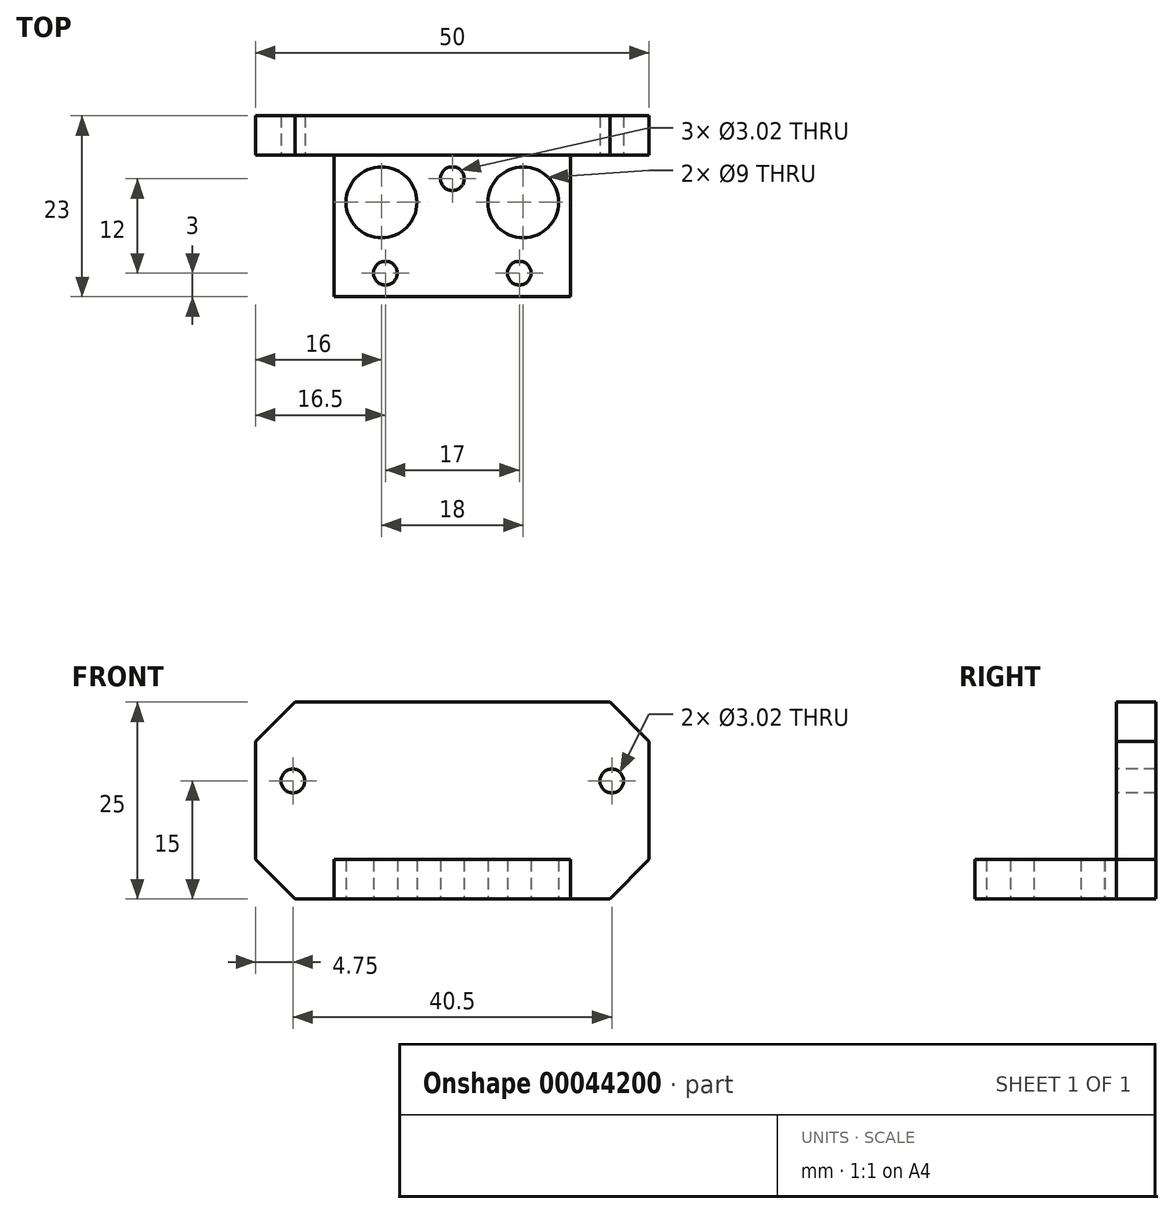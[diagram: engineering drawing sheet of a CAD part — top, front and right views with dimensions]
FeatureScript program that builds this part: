
annotation { "Feature Type Name" : "Feature", "Feature Type Description" : "" }
export const myFeature = defineFeature(function(context is Context, id is Id, definition is map)
    precondition{}
    {
        {
            var Q0;
            Q0=qCreatedBy(makeId("Top.planeOp"),FACE);
            var sketch = newSketch(context, id + "F0", { "sketchPlane" : qUnion([Q0])});
            skLineSegment(sketch, "E0.bottom", {"start": v(0, 0) * mm, "end": v(30, 0) * mm});
            skLineSegment(sketch, "E0.top", {"start": v(0, 18) * mm, "end": v(30, 18) * mm, "construction": true});
            skLineSegment(sketch, "E0.left", {"start": v(0, 0) * mm, "end": v(0, 18) * mm});
            skLineSegment(sketch, "E0.right", {"start": v(30, 0) * mm, "end": v(30, 18) * mm});
            skLineSegment(sketch, "E1", {"start": v(15, 18) * mm, "end": v(15, 15) * mm, "construction": true});
            skCircle(sketch, "E2", {"center": v(15, 15) * mm, "radius": 1.51 * mm});
            skLineSegment(sketch, "E3", {"start": v(15, 15) * mm, "end": v(15, 3) * mm, "construction": true});
            skLineSegment(sketch, "E4", {"start": v(15, 3) * mm, "end": v(23.5, 3) * mm, "construction": true});
            skLineSegment(sketch, "E5", {"start": v(15, 3) * mm, "end": v(6.5, 3) * mm, "construction": true});
            skLineSegment(sketch, "E6", {"start": v(15, 12) * mm, "end": v(24, 12) * mm, "construction": true});
            skLineSegment(sketch, "E7", {"start": v(15, 12) * mm, "end": v(6, 12) * mm, "construction": true});
            skLineSegment(sketch, "E8", {"start": v(24, 12) * mm, "end": v(24, 18) * mm, "construction": true});
            skCircle(sketch, "E9", {"center": v(6, 12) * mm, "radius": 4.5 * mm});
            skCircle(sketch, "E10", {"center": v(24, 12) * mm, "radius": 4.5 * mm});
            skCircle(sketch, "E11", {"center": v(23.5, 3) * mm, "radius": 1.51 * mm});
            skCircle(sketch, "E12", {"center": v(6.5, 3) * mm, "radius": 1.51 * mm});
            skLineSegment(sketch, "E13", {"start": v(0, 18) * mm, "end": v(0, 23) * mm});
            skLineSegment(sketch, "E14", {"start": v(0, 23) * mm, "end": v(29.76, 23) * mm});
            skLineSegment(sketch, "E15", {"start": v(29.76, 23) * mm, "end": v(30, 23) * mm});
            skLineSegment(sketch, "E16", {"start": v(30, 23) * mm, "end": v(30, 18) * mm});
            skSolve(sketch);
        }
        {
            var Q0;
            Q0 = qSketchRegion(id + "F0", true);
            var Q1;
            Q1=makeQuery(id+"F0.imprint","IMPRINT",FACE,{"disambiguationData":[TD([[makeQuery(id+"F0.imprint","IMPRINT",EDGE,{"derivedFrom":sQuery(id+"F0.wireOp",EDGE,"E0.bottom")}),1.0]])]});
            extrude(context, id + "F1", {"entities" : qUnion([Q0, Q1]), "depth" : 5 * mm});
        }
        {
            var Q0;
            Q0=makeQuery(id+"F1.opExtrude","CAP_FACE",FACE,{"disambiguationData":[OSD([sQuery(id+"F0.wireOp",EDGE,"E0.bottom"),sQuery(id+"F0.wireOp",EDGE,"E0.left"),sQuery(id+"F0.wireOp",EDGE,"E0.right"),sQuery(id+"F0.wireOp",EDGE,"E2"),sQuery(id+"F0.wireOp",EDGE,"E9"),sQuery(id+"F0.wireOp",EDGE,"E10"),sQuery(id+"F0.wireOp",EDGE,"E11"),sQuery(id+"F0.wireOp",EDGE,"E12"),sQuery(id+"F0.wireOp",EDGE,"E13"),sQuery(id+"F0.wireOp",EDGE,"E14"),sQuery(id+"F0.wireOp",EDGE,"E15"),sQuery(id+"F0.wireOp",EDGE,"E16")])],"isStart":false});
            var sketch = newSketch(context, id + "F2", { "sketchPlane" : qUnion([Q0])});
            skLineSegment(sketch, "E17.bottom", {"start": v(0, 23) * mm, "end": v(30, 23) * mm});
            skLineSegment(sketch, "E17.top", {"start": v(0, 18) * mm, "end": v(30, 18) * mm});
            skLineSegment(sketch, "E17.left", {"start": v(0, 23) * mm, "end": v(0, 18) * mm});
            skLineSegment(sketch, "E17.right", {"start": v(30, 23) * mm, "end": v(30, 18) * mm});
            skSolve(sketch);
        }
        {
            var Q0;
            Q0 = qSketchRegion(id + "F2", true);
            extrude(context, id + "F3", {"entities" : qUnion([Q0]), "operationType" : NewBodyOperationType.ADD, "depth" : 20 * mm});
        }
        {
            var Q0;
            Q0=makeQuery(id+"F3.boolean.opBoolean","MERGE",FACE,{"derivedFrom":[makeQuery(id+"F1.opExtrude","SWEPT_FACE",FACE,{"disambiguationData":[OSD([sQuery(id+"F0.wireOp",EDGE,"E0.left"),sQuery(id+"F0.wireOp",EDGE,"E13")])]}),makeQuery(id+"F3.opExtrude","SWEPT_FACE",FACE,{"disambiguationData":[OSD([sQuery(id+"F2.wireOp",EDGE,"E17.left")])]})]});
            var sketch = newSketch(context, id + "F4", { "sketchPlane" : qUnion([Q0])});
            skLineSegment(sketch, "E18.bottom", {"start": v(-23, 25) * mm, "end": v(-18, 25) * mm});
            skLineSegment(sketch, "E18.top", {"start": v(-23, 0) * mm, "end": v(-18, 0) * mm});
            skLineSegment(sketch, "E18.left", {"start": v(-23, 25) * mm, "end": v(-23, 0) * mm});
            skLineSegment(sketch, "E18.right", {"start": v(-18, 25) * mm, "end": v(-18, 0) * mm});
            skSolve(sketch);
        }
        {
            var Q0;
            Q0 = qSketchRegion(id + "F4", true);
            extrude(context, id + "F5", {"entities" : qUnion([Q0]), "operationType" : NewBodyOperationType.ADD, "depth" : 10 * mm});
        }
        {
            var Q0;
            Q0=makeQuery(id+"F3.boolean.opBoolean","MERGE",FACE,{"derivedFrom":[makeQuery(id+"F1.opExtrude","SWEPT_FACE",FACE,{"disambiguationData":[OSD([sQuery(id+"F0.wireOp",EDGE,"E0.right"),sQuery(id+"F0.wireOp",EDGE,"E16")])]}),makeQuery(id+"F3.opExtrude","SWEPT_FACE",FACE,{"disambiguationData":[OSD([sQuery(id+"F2.wireOp",EDGE,"E17.right")])]})]});
            var sketch = newSketch(context, id + "F6", { "sketchPlane" : qUnion([Q0])});
            skLineSegment(sketch, "E19.bottom", {"start": v(18, 25) * mm, "end": v(23, 25) * mm});
            skLineSegment(sketch, "E19.top", {"start": v(18, 0) * mm, "end": v(23, 0) * mm});
            skLineSegment(sketch, "E19.left", {"start": v(18, 25) * mm, "end": v(18, 0) * mm});
            skLineSegment(sketch, "E19.right", {"start": v(23, 25) * mm, "end": v(23, 0) * mm});
            skSolve(sketch);
        }
        {
            var Q0;
            Q0 = qSketchRegion(id + "F6", true);
            extrude(context, id + "F7", {"entities" : qUnion([Q0]), "operationType" : NewBodyOperationType.ADD, "depth" : 10 * mm});
        }
        {
            var Q0;
            Q0=makeQuery(id+"F7.boolean.opBoolean","MERGE",FACE,{"derivedFrom":[makeQuery(id+"F5.boolean.opBoolean","MERGE",FACE,{"derivedFrom":[makeQuery(id+"F3.opExtrude","SWEPT_FACE",FACE,{"disambiguationData":[OSD([sQuery(id+"F2.wireOp",EDGE,"E17.top")])]}),makeQuery(id+"F5.opExtrude","SWEPT_FACE",FACE,{"disambiguationData":[OSD([sQuery(id+"F4.wireOp",EDGE,"E18.right")])]})]}),makeQuery(id+"F7.opExtrude","SWEPT_FACE",FACE,{"disambiguationData":[OSD([sQuery(id+"F6.wireOp",EDGE,"E19.left")])]})]});
            var sketch = newSketch(context, id + "F8", { "sketchPlane" : qUnion([Q0])});
            skLineSegment(sketch, "E20", {"start": v(-10, 25) * mm, "end": v(-5, 25) * mm});
            skLineSegment(sketch, "E21", {"start": v(-5, 25) * mm, "end": v(-10, 20) * mm});
            skLineSegment(sketch, "E22", {"start": v(-10, 20) * mm, "end": v(-10, 25) * mm});
            skLineSegment(sketch, "E23", {"start": v(-10, 5) * mm, "end": v(-10, 0) * mm});
            skLineSegment(sketch, "E24", {"start": v(-10, 0) * mm, "end": v(-5, 0) * mm});
            skLineSegment(sketch, "E25", {"start": v(-5, 0) * mm, "end": v(-10, 5) * mm});
            skLineSegment(sketch, "E26", {"start": v(35, 0) * mm, "end": v(40, 0) * mm});
            skLineSegment(sketch, "E27", {"start": v(40, 0) * mm, "end": v(40, 5) * mm});
            skLineSegment(sketch, "E28", {"start": v(40, 5) * mm, "end": v(35, 0) * mm});
            skLineSegment(sketch, "E29", {"start": v(35, 25) * mm, "end": v(40, 25) * mm});
            skLineSegment(sketch, "E30", {"start": v(40, 25) * mm, "end": v(40, 20) * mm});
            skLineSegment(sketch, "E31", {"start": v(40, 20) * mm, "end": v(35, 25) * mm});
            skSolve(sketch);
        }
        {
            var Q0;
            Q0 = qSketchRegion(id + "F8", true);
            extrude(context, id + "F9", {"entities" : qUnion([Q0]), "operationType" : NewBodyOperationType.REMOVE, "endBound" : BoundingType.THROUGH_ALL, "oppositeDirection" : true, "depth" : 25 * mm});
        }
        {
            var Q0;
            Q0=makeQuery(id+"F7.boolean.opBoolean","MERGE",FACE,{"derivedFrom":[makeQuery(id+"F5.boolean.opBoolean","MERGE",FACE,{"derivedFrom":[makeQuery(id+"F3.opExtrude","SWEPT_FACE",FACE,{"disambiguationData":[OSD([sQuery(id+"F2.wireOp",EDGE,"E17.top")])]}),makeQuery(id+"F5.opExtrude","SWEPT_FACE",FACE,{"disambiguationData":[OSD([sQuery(id+"F4.wireOp",EDGE,"E18.right")])]})]}),makeQuery(id+"F7.opExtrude","SWEPT_FACE",FACE,{"disambiguationData":[OSD([sQuery(id+"F6.wireOp",EDGE,"E19.left")])]})]});
            var sketch = newSketch(context, id + "F10", { "sketchPlane" : qUnion([Q0])});
            skLineSegment(sketch, "E32", {"start": v(15, 25) * mm, "end": v(15, 15) * mm, "construction": true});
            skLineSegment(sketch, "E33", {"start": v(15, 15) * mm, "end": v(-5.25, 15) * mm, "construction": true});
            skLineSegment(sketch, "E34", {"start": v(15, 15) * mm, "end": v(35.25, 15) * mm, "construction": true});
            skCircle(sketch, "E35", {"center": v(-5.25, 15) * mm, "radius": 1.51 * mm});
            skCircle(sketch, "E36", {"center": v(35.25, 15) * mm, "radius": 1.51 * mm});
            skSolve(sketch);
        }
        {
            var Q0;
            Q0 = qSketchRegion(id + "F10", true);
            extrude(context, id + "F11", {"entities" : qUnion([Q0]), "operationType" : NewBodyOperationType.REMOVE, "endBound" : BoundingType.THROUGH_ALL, "oppositeDirection" : true, "depth" : 25 * mm});
        }
    });
